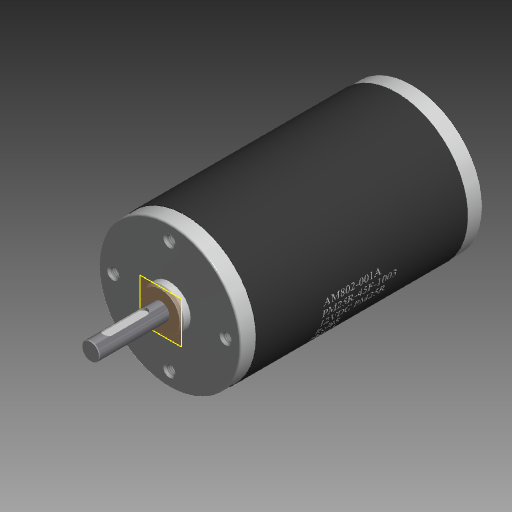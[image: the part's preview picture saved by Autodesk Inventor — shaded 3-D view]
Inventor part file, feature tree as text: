
AUTODESK INVENTOR PART (.ipt)
format: ipt  version: 2017.1 (Build 211199000, 199)  size: 7,304,704 bytes
history: native  units: mm (DEFAULTED — no unit token found)
features: sketch x10, extrude x7, chamfer x4, plane x3, hole x2, pattern_circular x2, fillet x2, emboss x1, split x1
ambient origin geometry x8: Origin, YZ Plane, XZ Plane, XY Plane, X Axis, Y Axis, Z Axis, Center Point
bodies: Solid1 (feature_tree), Solid2 (feature_tree), Solid3 (feature_tree)
feature tree (32):
  extrude  "Extrusion1"  Depth=7.0mm TaperAngle=0.0deg
  extrude  "Extrusion2"  Depth=3.9878mm TaperAngle=0.0deg
  chamfer  "Chamfer1"  Distance=1.0mm
  hole  "Hole2"  [1 undecoded]
  pattern_circular  "Circular Pattern2"  Count=4 Angle=90.0deg
  chamfer  "Chamfer3"  Distance=31.623mm
  extrude  "Extrusion3"  Depth=12.7mm
  fillet  "Fillet1"  Radius=64.4144mm
  extrude  "Extrusion5"  Depth=64.008mm
  extrude  "Extrusion6"  Depth=7.0mm
  extrude  "Extrusion7"  Depth=0.508mm
  hole  "Hole3"  [1 undecoded]
  chamfer  "Chamfer2"  Distance=20.0mm Angle=360.0deg
  pattern_circular  "Circular Pattern3"  [2 undecoded]
  fillet  "Fillet2"  [1 undecoded]
  chamfer  "Chamfer4"  Distance=1.99898mm
  plane  "Work Plane1"
  extrude  "Extrusion8"  Depth=1.99898mm
  plane  "Work Plane2"
  emboss  "Emboss1"
  plane  "Work Plane3"
  split  "Split1"
  sketch  "Sketch1"  dims[d0=64.008mm d1=7.0mm d2=0.0mm]
  sketch  "Sketch2"  dims[d3=19.05mm d4=3.9878mm d5=0.0mm d6=1.0mm d7=1.0mm]
  sketch  "Sketch4"  dims[d18=3.9624mm d19=9.525mm d20=6.35mm d21=60.0deg d22=19.05mm d23=20.594885mm d24=25.4mm d25=40.0mm d27=90.0deg]
  sketch  "Sketch5"  dims[d28=7.9502mm d29=31.623mm d30=0.0mm]
  sketch  "Sketch8"  dims[d31=0.79375mm d33=12.7mm d38=64.4144mm]
  sketch  "Sketch9"  dims[d39=95.6056mm d40=0.0mm d41=64.008mm]
  sketch  "Sketch10"  dims[d42=7.0mm d43=0.0mm d44=30.1498mm]
  sketch  "Sketch11"  dims[d45=4.1148mm d46=0.0mm]
  sketch  "Sketch12"  dims[d47=5.08mm d48=12.7mm d49=9.906mm d50=4.572mm d51=14.3117mm d52=7.62mm d53=20.594885mm d54=0.508mm d55=3.175mm]
  sketch  "Sketch13"  dims[d56=0.762mm d57=0.762mm d58=3.175mm d59=20.0mm d61=360.0deg d62=0.25mm d63=3.175mm d64=45.0deg d65=45.0deg d66=45.0deg d67=45.0deg d68=1.99898mm d70=20.09902mm d71=7.99338mm d72=1.15062mm d73=0.0mm d74=30.48mm d75=0.0254mm d76=0.0mm d77=0.0mm]
note: 5 required parameter values undecoded (feature->parameter linkage not recoverable at this tier; creation-order binding heuristic only, values carry confidence <= 0.55)
